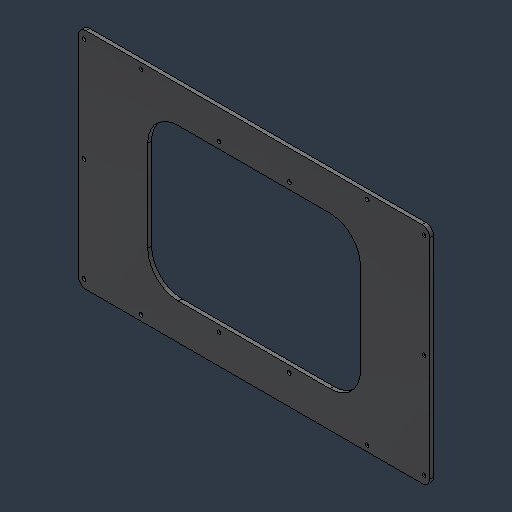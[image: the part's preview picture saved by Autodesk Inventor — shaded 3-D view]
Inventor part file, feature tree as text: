
AUTODESK INVENTOR PART (.ipt)
format: ipt  version: 2024.3 (Build 283343000, 343)  size: 114,688 bytes
history: native  units: mm (DEFAULTED — no unit token found)
features: fillet x1
ambient origin geometry x8: Origin, YZ Plane, XZ Plane, XY Plane, X Axis, Y Axis, Z Axis, Center Point
bodies: Solid1 (feature_tree)
feature tree (1):
  fillet  "Fillet2"  [1 undecoded]
note: 1 required parameter value undecoded (feature->parameter linkage not recoverable at this tier; creation-order binding heuristic only, values carry confidence <= 0.55)
